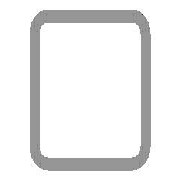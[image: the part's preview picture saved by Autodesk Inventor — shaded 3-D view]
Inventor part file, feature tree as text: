
AUTODESK INVENTOR PART (.ipt)
format: ipt  version: 2025 (Build 290162010, 162A)  size: 130,048 bytes
history: native  units: mm (DEFAULTED — no unit token found)
features: other x3, sketch x1, plane x1
ambient origin geometry x8: Origin, YZ Plane, XZ Plane, XY Plane, X Axis, Y Axis, Z Axis, Center Point
bodies: Solid1 (feature_tree), Body (feature_tree)
feature tree (5):
  other  "Driven Length"
  other  "Start plane"
  other  "End plane"
  sketch  "Sketch3"  dims[d3=898.0mm d4=0.0mm d7=4.0mm d9=40.0mm d11=40.0mm d12=2.0mm d13=-0.0mm d14=898.0mm d15=20.0mm d16=20.0mm d17=90.0deg d18=898.0mm]
  plane  "Work Plane3"
